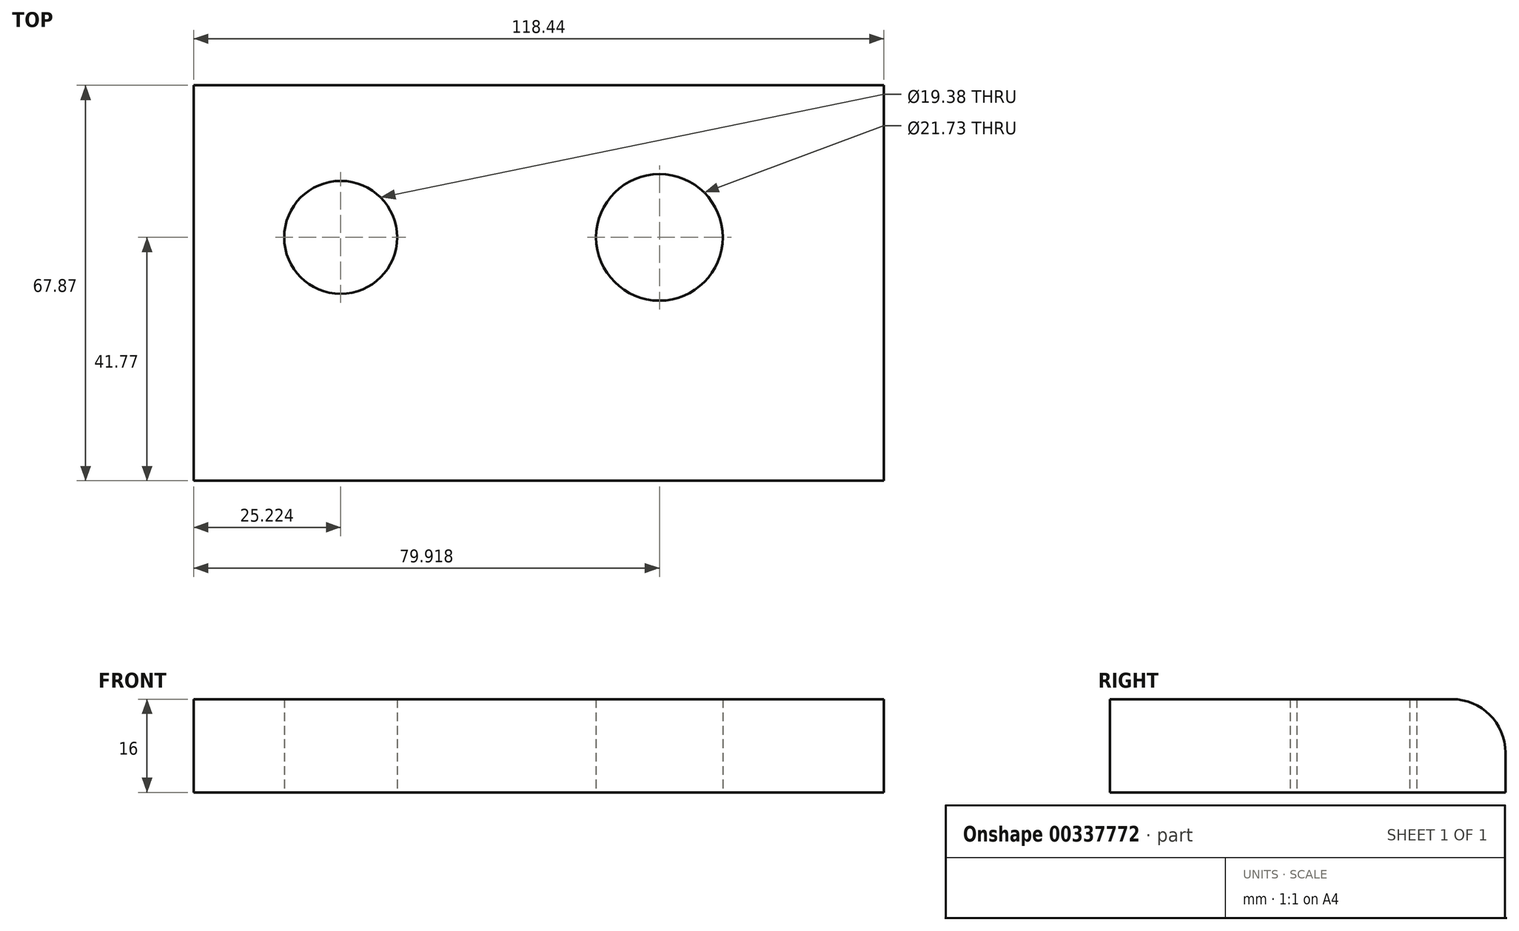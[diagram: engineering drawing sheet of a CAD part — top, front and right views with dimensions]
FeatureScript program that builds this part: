
annotation { "Feature Type Name" : "Feature", "Feature Type Description" : "" }
export const myFeature = defineFeature(function(context is Context, id is Id, definition is map)
    precondition{}
    {
        {
            var Q0;
            Q0=qCreatedBy(makeId("Top.planeOp"),FACE);
            var sketch = newSketch(context, id + "F0", { "sketchPlane" : qUnion([Q0])});
            skLineSegment(sketch, "E0.bottom", {"start": v(-61.32, 26.1) * mm, "end": v(57.12, 26.1) * mm});
            skLineSegment(sketch, "E0.top", {"start": v(-61.32, -41.77) * mm, "end": v(57.12, -41.77) * mm});
            skLineSegment(sketch, "E0.left", {"start": v(-61.32, 26.1) * mm, "end": v(-61.32, -41.77) * mm});
            skLineSegment(sketch, "E0.right", {"start": v(57.12, 26.1) * mm, "end": v(57.12, -41.77) * mm});
            skCircle(sketch, "E1", {"center": v(-36.1, 0) * mm, "radius": 9.7 * mm});
            skCircle(sketch, "E2", {"center": v(18.6, 0) * mm, "radius": 10.87 * mm});
            skSolve(sketch);
        }
        {
            var Q0;
            Q0 = qSketchRegion(id + "F0", true);
            extrude(context, id + "F1", {"entities" : qUnion([Q0]), "depth" : 16 * mm});
        }
        {
            var Q0;
            Q0=makeQuery(id+"F1.opExtrude","CAP_EDGE",EDGE,{"disambiguationData":[OSD([sQuery(id+"F0.wireOp",EDGE,"E0.bottom")])],"isStart":false});
            fillet(context, id + "F2", {"entities" : qUnion([Q0]), "radius" : 9.2 * mm, "tangentPropagation" : true, "allowEdgeOverflow" : false});
        }
    });
